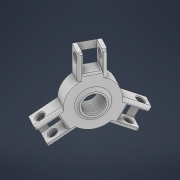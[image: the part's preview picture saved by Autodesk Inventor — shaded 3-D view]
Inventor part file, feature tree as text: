
AUTODESK INVENTOR PART (.ipt)
format: ipt  version: 2022 (Build 260153000, 153)  size: 294,912 bytes
history: native  units: in
note: dims shown in document units (in); Inventor stores cm internally (conversion verified against a paired STEP export)
features: other x2, thread x1
ambient origin geometry x8: Origin, YZ Plane, XZ Plane, XY Plane, X Axis, Y Axis, Z Axis, Center Point
bodies: Solid1 (feature_tree)
feature tree (3):
  other  "Gyrodesignv2editneeded - Copy.iam"
  other  "Gyrocopter Base.ipt:1"
  thread  "Thread1"  [1 undecoded]
note: 1 required parameter value undecoded (feature->parameter linkage not recoverable at this tier; creation-order binding heuristic only, values carry confidence <= 0.55)
